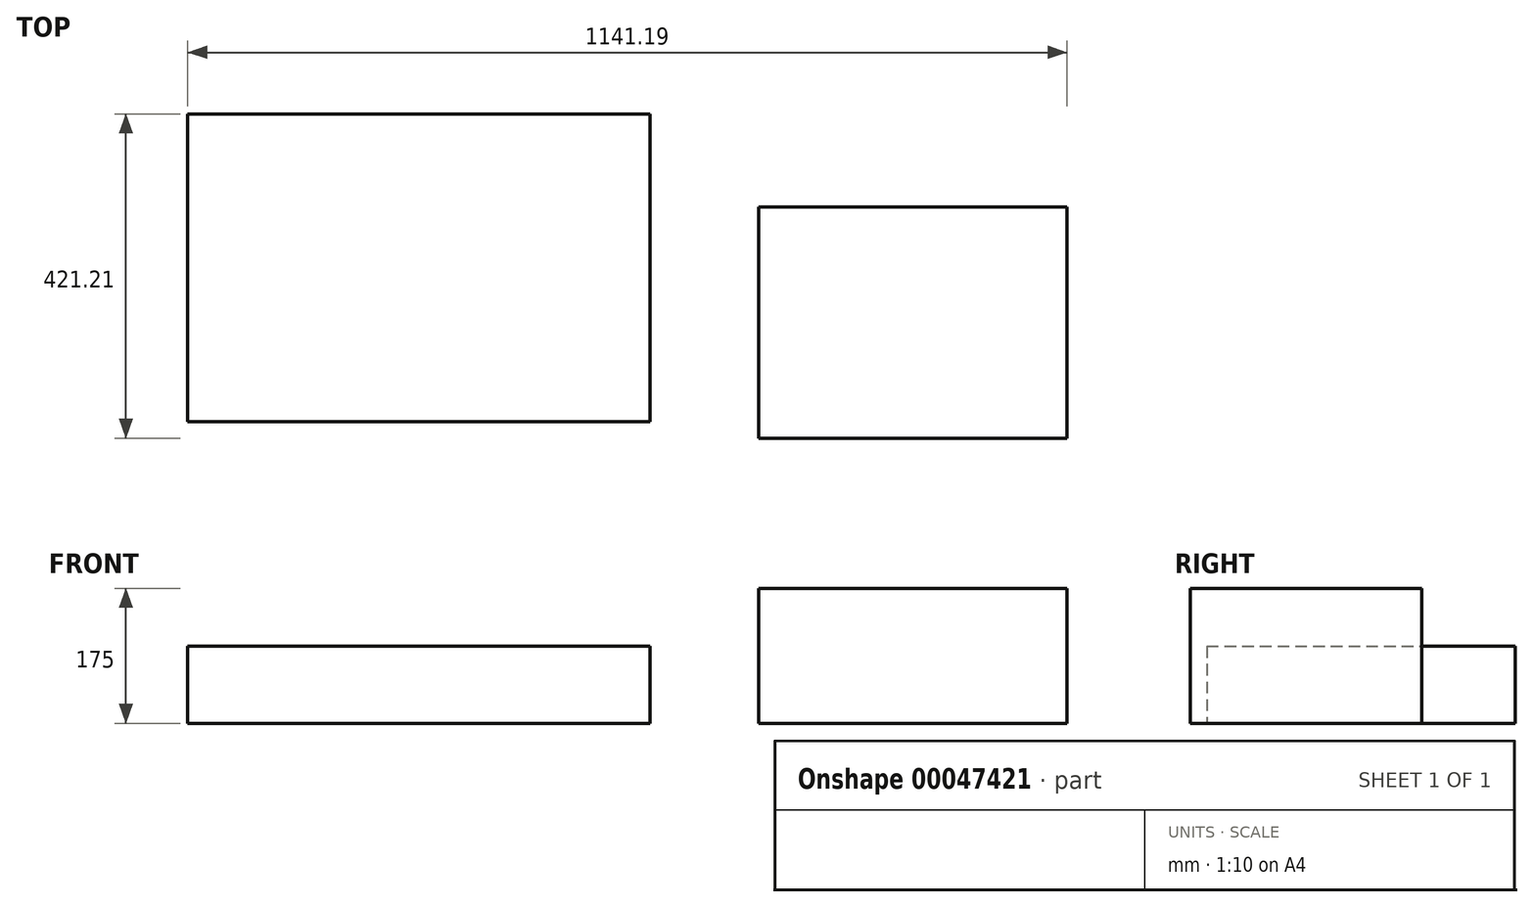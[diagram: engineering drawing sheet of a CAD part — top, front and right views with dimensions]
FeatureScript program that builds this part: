
annotation { "Feature Type Name" : "Feature", "Feature Type Description" : "" }
export const myFeature = defineFeature(function(context is Context, id is Id, definition is map)
    precondition{}
    {
        {
            var Q0;
            Q0=qCreatedBy(makeId("Top.planeOp"),FACE);
            var sketch = newSketch(context, id + "F0", { "sketchPlane" : qUnion([Q0])});
            skLineSegment(sketch, "E0.rect.bottom", {"start": v(520.2, -234.45) * mm, "end": v(920.2, -234.45) * mm});
            skLineSegment(sketch, "E0.rect.top", {"start": v(520.2, 65.55) * mm, "end": v(920.2, 65.55) * mm});
            skLineSegment(sketch, "E0.rect.left", {"start": v(520.2, -234.45) * mm, "end": v(520.2, 65.55) * mm});
            skLineSegment(sketch, "E0.rect.right", {"start": v(920.2, -234.45) * mm, "end": v(920.2, 65.55) * mm});
            skPoint(sketch, "E0.rect.middle", {"position": v(720.2, -84.45) * mm});
            skLineSegment(sketch, "E1.rect.bottom", {"start": v(379.02, -213.24) * mm, "end": v(-220.98, -213.24) * mm});
            skLineSegment(sketch, "E1.rect.top", {"start": v(379.02, 186.76) * mm, "end": v(-220.98, 186.76) * mm});
            skLineSegment(sketch, "E1.rect.left", {"start": v(379.02, -213.24) * mm, "end": v(379.02, 186.76) * mm});
            skLineSegment(sketch, "E1.rect.right", {"start": v(-220.98, -213.24) * mm, "end": v(-220.98, 186.76) * mm});
            skPoint(sketch, "E1.rect.middle", {"position": v(79.02, -13.24) * mm});
            skSolve(sketch);
        }
        {
            var Q0;
            Q0=makeQuery(id+"F0.imprint","IMPRINT",FACE,{"disambiguationData":[TD([[makeQuery(id+"F0.imprint","IMPRINT",EDGE,{"derivedFrom":sQuery(id+"F0.wireOp",EDGE,"E0.rect.bottom")}),1.0]])]});
            extrude(context, id + "F1", {"entities" : qUnion([Q0]), "depth" : 175 * mm});
        }
        {
            var Q0;
            Q0=makeQuery(id+"F0.imprint","IMPRINT",FACE,{"disambiguationData":[TD([[makeQuery(id+"F0.imprint","IMPRINT",EDGE,{"derivedFrom":sQuery(id+"F0.wireOp",EDGE,"E1.rect.bottom")}),-1.0]])]});
            extrude(context, id + "F2", {"entities" : qUnion([Q0]), "depth" : 100 * mm});
        }
    });
